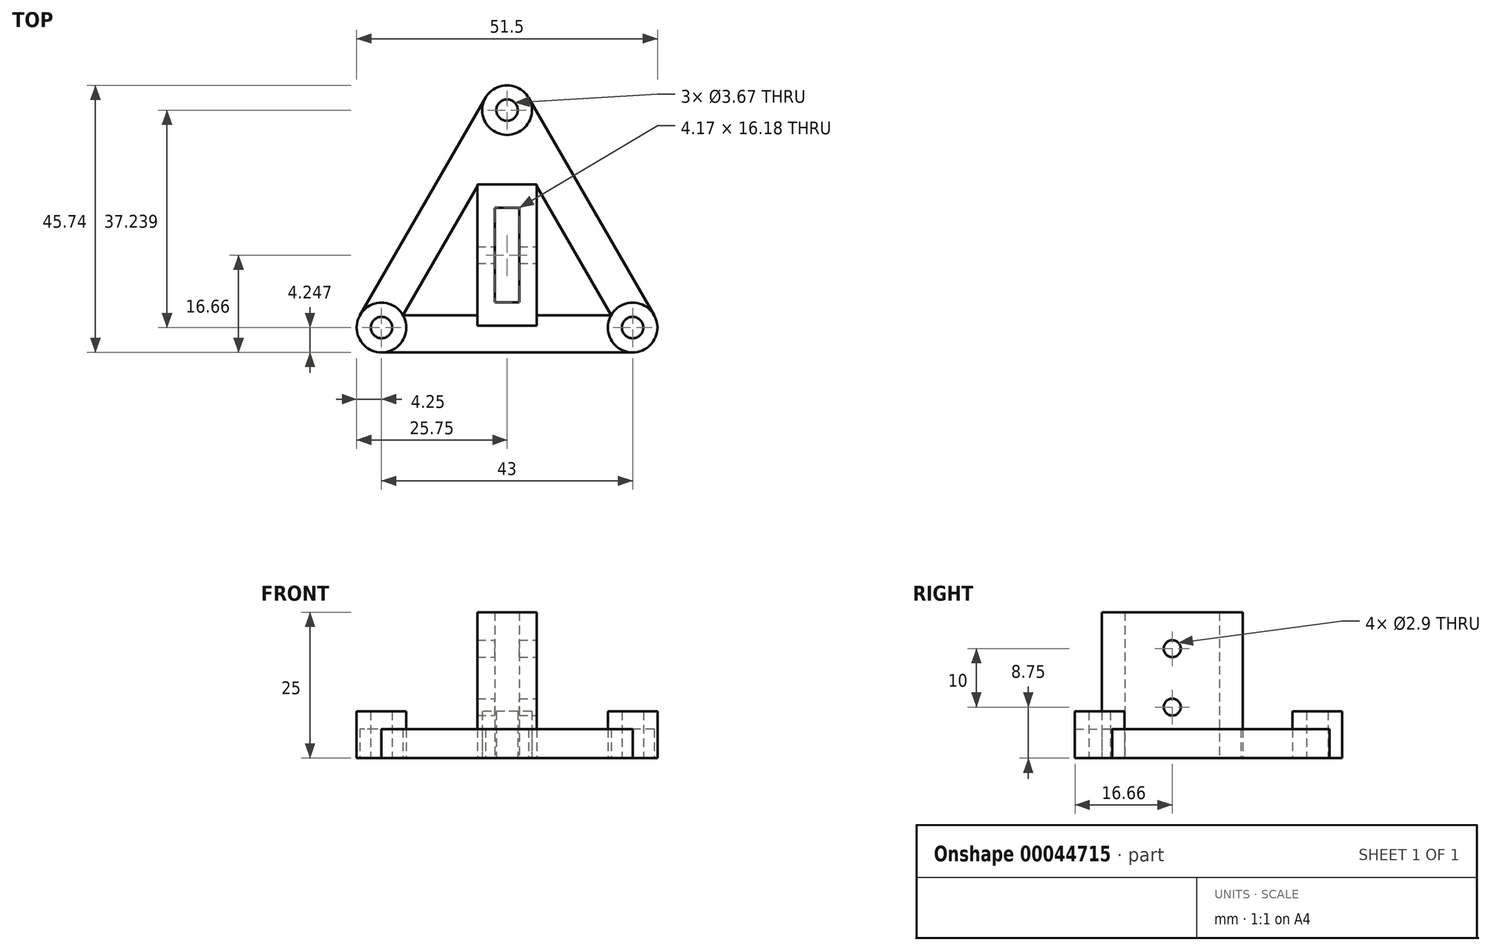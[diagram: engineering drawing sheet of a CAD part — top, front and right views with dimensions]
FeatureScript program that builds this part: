
annotation { "Feature Type Name" : "Feature", "Feature Type Description" : "" }
export const myFeature = defineFeature(function(context is Context, id is Id, definition is map)
    precondition{}
    {
        {
            var Q0;
            Q0=qCreatedBy(makeId("Top.planeOp"),FACE);
            var sketch = newSketch(context, id + "F3", { "sketchPlane" : qUnion([Q0])});
            skCircle(sketch, "E0", {"center": v(21.5, -12.41) * mm, "radius": 4.25 * mm});
            skCircle(sketch, "E1", {"center": v(0, 24.83) * mm, "radius": 4.25 * mm});
            skCircle(sketch, "E2", {"center": v(-21.5, -12.41) * mm, "radius": 4.25 * mm});
            skLineSegment(sketch, "E3", {"start": v(21.5, -16.66) * mm, "end": v(-21.5, -16.66) * mm});
            skLineSegment(sketch, "E4", {"start": v(-21.5, -16.66) * mm, "end": v(-21.5, -16.66) * mm});
            skLineSegment(sketch, "E5", {"start": v(-3.68, 26.95) * mm, "end": v(-25.18, -10.29) * mm});
            skLineSegment(sketch, "E6", {"start": v(25.18, -10.29) * mm, "end": v(3.68, 26.95) * mm});
            skCircle(sketch, "E7", {"center": v(-21.5, -12.41) * mm, "radius": 1.84 * mm});
            skCircle(sketch, "E8", {"center": v(21.5, -12.41) * mm, "radius": 1.84 * mm});
            skCircle(sketch, "E9", {"center": v(0, 24.83) * mm, "radius": 1.84 * mm});
            skPoint(sketch, "E10.rect.middle", {"position": v(0, 0) * mm});
            skLineSegment(sketch, "E11", {"start": v(0, 0) * mm, "end": v(21.5, -12.41) * mm, "construction": true});
            skLineSegment(sketch, "E12", {"start": v(0, 0) * mm, "end": v(-21.5, -12.41) * mm, "construction": true});
            skLineSegment(sketch, "E13", {"start": v(0, 0) * mm, "end": v(0, 24.83) * mm, "construction": true});
            skLineSegment(sketch, "E14", {"start": v(5.09, 11.76) * mm, "end": v(17.82, -10.29) * mm});
            skLineSegment(sketch, "E15", {"start": v(-17.82, -10.29) * mm, "end": v(-5.09, 11.76) * mm});
            skLineSegment(sketch, "E16.rect.bottom", {"start": v(2.09, 8.09) * mm, "end": v(-2.09, 8.09) * mm});
            skLineSegment(sketch, "E16.rect.top", {"start": v(2.09, -8.09) * mm, "end": v(-2.09, -8.09) * mm});
            skLineSegment(sketch, "E16.rect.left", {"start": v(2.09, 8.09) * mm, "end": v(2.09, -8.09) * mm});
            skLineSegment(sketch, "E16.rect.right", {"start": v(-2.09, 8.09) * mm, "end": v(-2.09, -8.09) * mm});
            skLineSegment(sketch, "E17", {"start": v(-17.82, -10.29) * mm, "end": v(-5.09, -10.29) * mm});
            skLineSegment(sketch, "E18.rect.bottom", {"start": v(5.09, 12.09) * mm, "end": v(-5.09, 12.09) * mm});
            skLineSegment(sketch, "E18.rect.top", {"start": v(5.09, -12.09) * mm, "end": v(-5.09, -12.09) * mm});
            skLineSegment(sketch, "E18.rect.left", {"start": v(5.09, 12.09) * mm, "end": v(5.09, -12.09) * mm});
            skLineSegment(sketch, "E18.rect.right", {"start": v(-5.09, 12.09) * mm, "end": v(-5.09, -12.09) * mm});
            skLineSegment(sketch, "E19.trimOffspring", {"start": v(5.09, -10.29) * mm, "end": v(17.82, -10.29) * mm});
            skSolve(sketch);
        }
        {
            var Q0;
            {var subQ5=sQuery(id+"F3.wireOp",EDGE,"E3");Q0=makeQuery(id+"F3.imprint","IMPRINT",FACE,{"disambiguationData":[TD([[makeQuery(id+"F3.imprint","IMPRINT",EDGE,{"derivedFrom":subQ5}),-1.0]])]});}
            var Q1;
            {var subQ7=sQuery(id+"F3.wireOp",EDGE,"E5");Q1=makeQuery(id+"F3.imprint","IMPRINT",FACE,{"disambiguationData":[TD([[makeQuery(id+"F3.imprint","IMPRINT",EDGE,{"derivedFrom":subQ7}),1.0]])]});}
            extrude(context, id + "F0", {"entities" : qUnion([Q0, Q1]), "depth" : 5 * mm});
        }
        {
            var Q0;
            Q0=makeQuery(id+"F3.imprint","IMPRINT",FACE,{"disambiguationData":[TD([[makeQuery(id+"F3.imprint","IMPRINT",EDGE,{"derivedFrom":sQuery(id+"F3.wireOp",EDGE,"E8")}),-1.0]])]});
            var Q1;
            Q1=makeQuery(id+"F3.imprint","IMPRINT",FACE,{"disambiguationData":[TD([[makeQuery(id+"F3.imprint","IMPRINT",EDGE,{"derivedFrom":sQuery(id+"F3.wireOp",EDGE,"E9")}),-1.0]])]});
            var Q2;
            Q2=makeQuery(id+"F3.imprint","IMPRINT",FACE,{"disambiguationData":[TD([[makeQuery(id+"F3.imprint","IMPRINT",EDGE,{"derivedFrom":sQuery(id+"F3.wireOp",EDGE,"E7")}),-1.0]])]});
            extrude(context, id + "F4", {"entities" : qUnion([Q0, Q1, Q2]), "depth" : 8 * mm});
        }
        {
            var Q0;
            Q0=makeQuery(id+"F3.imprint","IMPRINT",FACE,{"disambiguationData":[TD([[makeQuery(id+"F3.imprint","IMPRINT",EDGE,{"derivedFrom":sQuery(id+"F3.wireOp",EDGE,"E16.rect.bottom")}),-1.0]])]});
            extrude(context, id + "F1", {"entities" : qUnion([Q0]), "depth" : 25 * mm});
        }
        {
            var Q0;
            Q0=makeQuery(id+"F1.opExtrude","SWEPT_FACE",FACE,{"disambiguationData":[OSD([sQuery(id+"F3.wireOp",EDGE,"E18.rect.left")])]});
            var sketch = newSketch(context, id + "F5", { "sketchPlane" : qUnion([Q0])});
            skLineSegment(sketch, "E20", {"start": v(0, 25) * mm, "end": v(0, 0) * mm, "construction": true});
            skLineSegment(sketch, "E21", {"start": v(12.09, 12.5) * mm, "end": v(-12.09, 12.5) * mm, "construction": true});
            skCircle(sketch, "E22", {"center": v(0, 18.75) * mm, "radius": 1.45 * mm});
            skCircle(sketch, "E23", {"center": v(0, 8.75) * mm, "radius": 1.45 * mm});
            skPoint(sketch, "E24", {"position": v(0, 12.5) * mm});
            skSolve(sketch);
        }
        {
            var Q0;
            Q0=sQuery(id+"F5.wireOp",VERTEX,"E22.center");
            var Q1;
            Q1=makeQuery(id+"F1.opExtrude","SWEPT_BODY",BODY,{"disambiguationData":[OSD([sQuery(id+"F3.wireOp",EDGE,"E16.rect.bottom"),sQuery(id+"F3.wireOp",EDGE,"E16.rect.top"),sQuery(id+"F3.wireOp",EDGE,"E16.rect.left"),sQuery(id+"F3.wireOp",EDGE,"E16.rect.right"),sQuery(id+"F3.wireOp",EDGE,"E18.rect.bottom"),sQuery(id+"F3.wireOp",EDGE,"E18.rect.top"),sQuery(id+"F3.wireOp",EDGE,"E18.rect.left"),sQuery(id+"F3.wireOp",EDGE,"E18.rect.right")])]});
            hole(context, id + "F2", {"style" : HoleStyle.SIMPLE, "holeDiameter" : 2.9 * mm, "endStyle" : HoleEndStyle.THROUGH, "locations" : qUnion([Q0]), "scope" : qUnion([Q1])});
        }
        {
            var Q0;
            Q0=sQuery(id+"F5.wireOp",VERTEX,"E23.center");
            var Q1;
            Q1=makeQuery(id+"F1.opExtrude","SWEPT_BODY",BODY,{"disambiguationData":[OSD([sQuery(id+"F3.wireOp",EDGE,"E16.rect.bottom"),sQuery(id+"F3.wireOp",EDGE,"E16.rect.top"),sQuery(id+"F3.wireOp",EDGE,"E16.rect.left"),sQuery(id+"F3.wireOp",EDGE,"E16.rect.right"),sQuery(id+"F3.wireOp",EDGE,"E18.rect.bottom"),sQuery(id+"F3.wireOp",EDGE,"E18.rect.top"),sQuery(id+"F3.wireOp",EDGE,"E18.rect.left"),sQuery(id+"F3.wireOp",EDGE,"E18.rect.right")])]});
            hole(context, id + "F6", {"style" : HoleStyle.SIMPLE, "holeDiameter" : 2.9 * mm, "endStyle" : HoleEndStyle.THROUGH, "locations" : qUnion([Q0]), "scope" : qUnion([Q1])});
        }
    });
